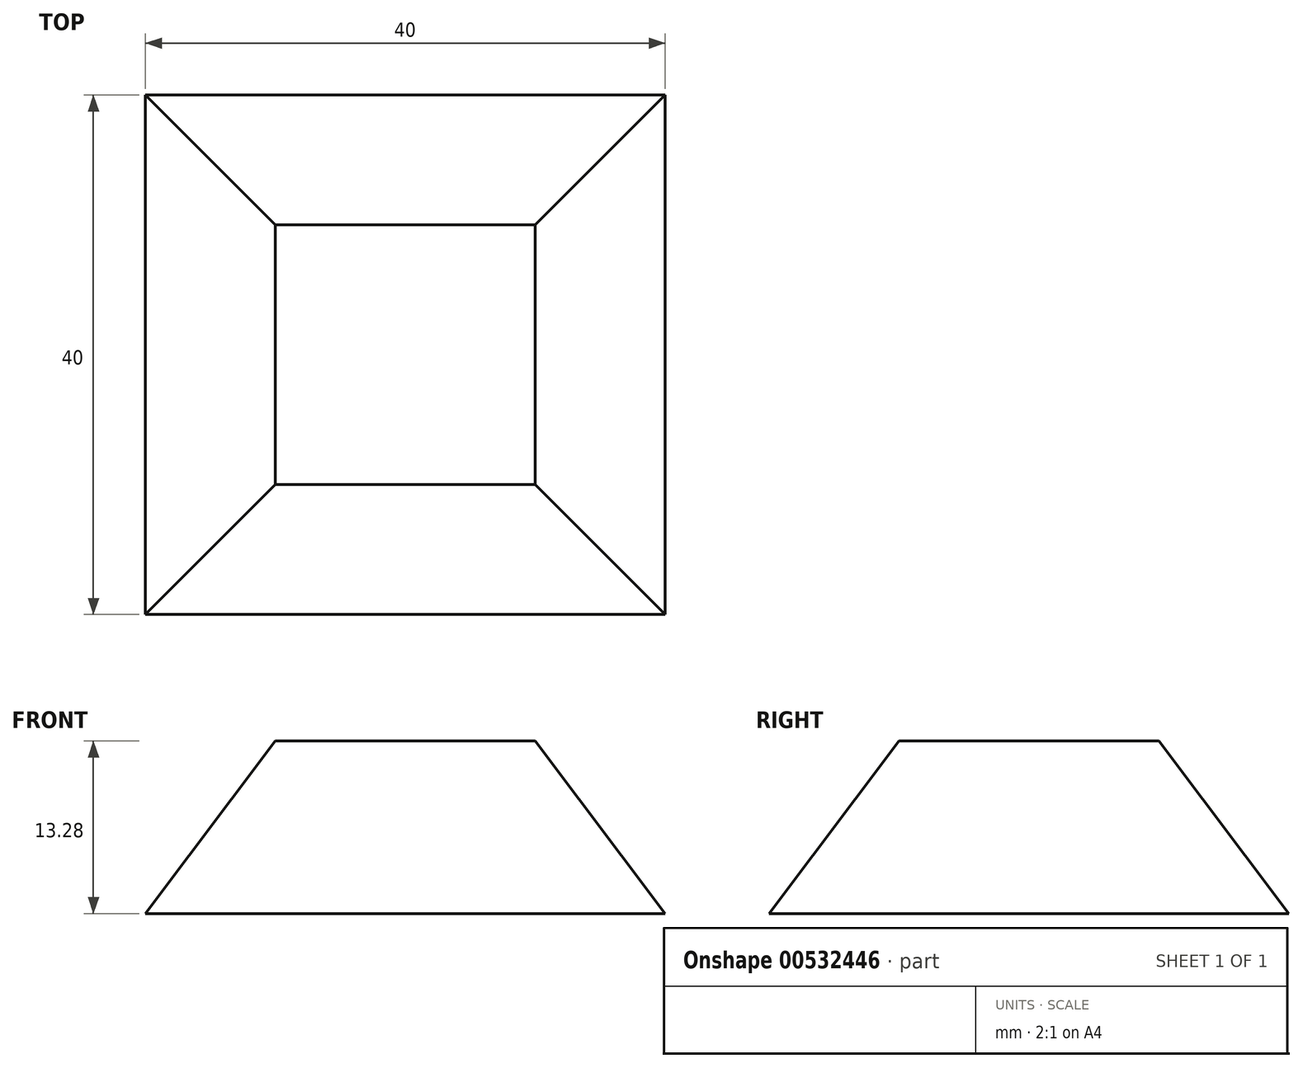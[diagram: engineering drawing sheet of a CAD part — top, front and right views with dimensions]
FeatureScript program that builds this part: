
annotation { "Feature Type Name" : "Feature", "Feature Type Description" : "" }
export const myFeature = defineFeature(function(context is Context, id is Id, definition is map)
    precondition{}
    {
        {
            var Q0;
            Q0=qCreatedBy(makeId("Top.planeOp"),FACE);
            var sketch = newSketch(context, id + "F0", { "sketchPlane" : qUnion([Q0])});
            skLineSegment(sketch, "E0.bottom", {"start": v(20, -20) * mm, "end": v(-20, -20) * mm});
            skLineSegment(sketch, "E0.top", {"start": v(20, 20) * mm, "end": v(-20, 20) * mm});
            skLineSegment(sketch, "E0.left", {"start": v(20, -20) * mm, "end": v(20, 20) * mm});
            skLineSegment(sketch, "E0.right", {"start": v(-20, -20) * mm, "end": v(-20, 20) * mm});
            skPoint(sketch, "E0.middle", {"position": v(0, 0) * mm});
            skSolve(sketch);
        }
        {
            var Q0;
            Q0=qCreatedBy(makeId("Top.planeOp"),FACE);
            cPlane(context, id + "F1", {"entities" : qUnion([Q0]), "cplaneType" : CPlaneType.OFFSET, "offset" : 13.28 * mm, "width" : 152.4 * mm, "height" : 152.4 * mm});
        }
        {
            var Q0;
            Q0=qCreatedBy(id+"F1.planeOp",FACE);
            var sketch = newSketch(context, id + "F2", { "sketchPlane" : qUnion([Q0])});
            skLineSegment(sketch, "E1.bottom", {"start": v(10, -10) * mm, "end": v(-10, -10) * mm});
            skLineSegment(sketch, "E1.top", {"start": v(10, 10) * mm, "end": v(-10, 10) * mm});
            skLineSegment(sketch, "E1.left", {"start": v(10, -10) * mm, "end": v(10, 10) * mm});
            skLineSegment(sketch, "E1.right", {"start": v(-10, -10) * mm, "end": v(-10, 10) * mm});
            skPoint(sketch, "E1.middle", {"position": v(0, 0) * mm});
            skSolve(sketch);
        }
        {
            var Q0;
            Q0 = qSketchRegion(id + "F0", true);
            var Q1;
            Q1 = qSketchRegion(id + "F2", true);
            loft(context, id + "F3", {"sheetProfilesArray" : [{ "sheetProfileEntities" : qUnion([Q0]) }, { "sheetProfileEntities" : qUnion([Q1]) }]});
        }
    });
